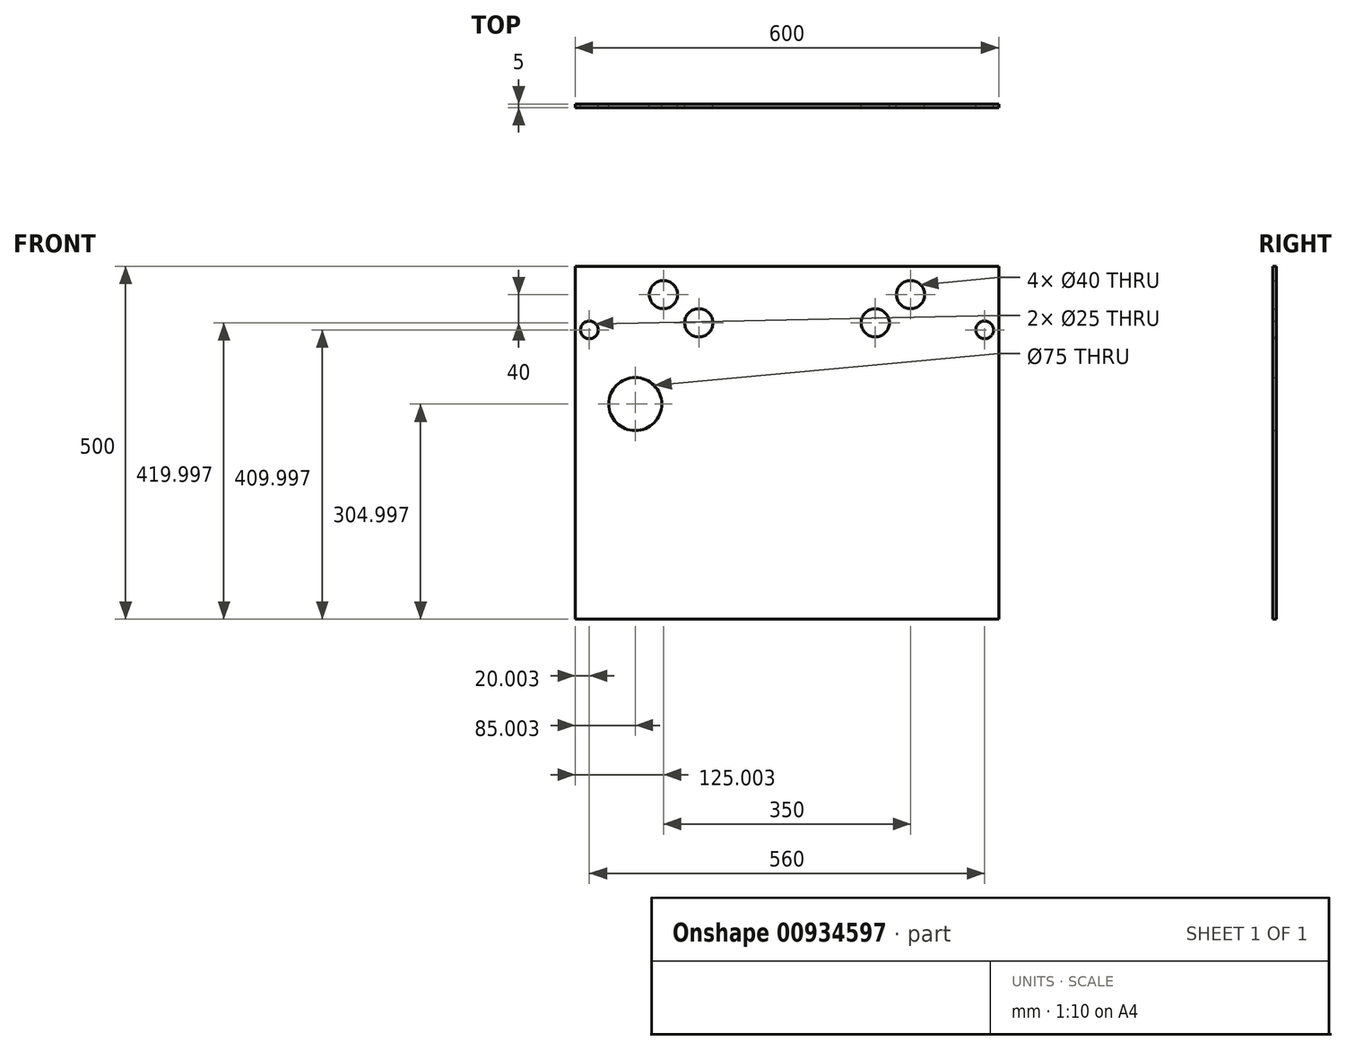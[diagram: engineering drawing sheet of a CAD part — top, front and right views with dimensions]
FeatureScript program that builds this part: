
annotation { "Feature Type Name" : "Feature", "Feature Type Description" : "" }
export const myFeature = defineFeature(function(context is Context, id is Id, definition is map)
    precondition{}
    {
        {
            var Q0;
            Q0=qCreatedBy(makeId("Front.planeOp"),FACE);
            var sketch = newSketch(context, id + "F0", { "sketchPlane" : qUnion([Q0])});
            skLineSegment(sketch, "E0.bottom", {"start": v(57.23, 19.9) * mm, "end": v(-542.77, 19.9) * mm});
            skLineSegment(sketch, "E0.top", {"start": v(57.23, 519.9) * mm, "end": v(-542.77, 519.9) * mm});
            skLineSegment(sketch, "E0.left", {"start": v(57.23, 19.9) * mm, "end": v(57.23, 519.9) * mm});
            skLineSegment(sketch, "E0.right", {"start": v(-542.77, 19.9) * mm, "end": v(-542.77, 519.9) * mm});
            skCircle(sketch, "E1", {"center": v(-417.77, 479.9) * mm, "radius": 20 * mm});
            skCircle(sketch, "E2", {"center": v(-367.77, 439.9) * mm, "radius": 20 * mm});
            skCircle(sketch, "E3", {"center": v(-522.77, 429.9) * mm, "radius": 12.5 * mm});
            skLineSegment(sketch, "E4", {"start": v(-242.77, 19.9) * mm, "end": v(-242.77, 519.9) * mm, "construction": true});
            skCircle(sketch, "E5.MirrorC", {"center": v(-117.77, 439.9) * mm, "radius": 20 * mm});
            skCircle(sketch, "E6.MirrorC", {"center": v(-67.77, 479.9) * mm, "radius": 20 * mm});
            skCircle(sketch, "E7.MirrorC", {"center": v(37.23, 429.9) * mm, "radius": 12.5 * mm});
            skCircle(sketch, "E8", {"center": v(-457.77, 324.9) * mm, "radius": 37.5 * mm});
            skLineSegment(sketch, "E9", {"start": v(-542.77, 399.9) * mm, "end": v(57.23, 399.9) * mm, "construction": true});
            skPoint(sketch, "E10", {"position": v(-456.63, 362.38) * mm});
            skPoint(sketch, "E11", {"position": v(37.07, 417.4) * mm});
            skPoint(sketch, "E12", {"position": v(-522.6, 417.4) * mm});
            skLineSegment(sketch, "E13", {"start": v(-522.6, 417.4) * mm, "end": v(-456.63, 362.38) * mm});
            skLineSegment(sketch, "E14", {"start": v(37.07, 417.4) * mm, "end": v(-456.63, 362.38) * mm});
            skLineSegment(sketch, "E15", {"start": v(-542.77, 59.9) * mm, "end": v(57.23, 59.9) * mm, "construction": true});
            skLineSegment(sketch, "E16", {"start": v(-502.77, 519.9) * mm, "end": v(-502.77, 19.9) * mm, "construction": true});
            skLineSegment(sketch, "E17.MirrorCS", {"start": v(17.23, 519.9) * mm, "end": v(17.23, 19.9) * mm, "construction": true});
            skSolve(sketch);
        }
        {
            var Q0;
            Q0 = qSketchRegion(id + "F0", true);
            extrude(context, id + "F1", {"entities" : qUnion([Q0]), "depth" : 5 * mm, "offsetDistance" : 25 * mm});
        }
    });
